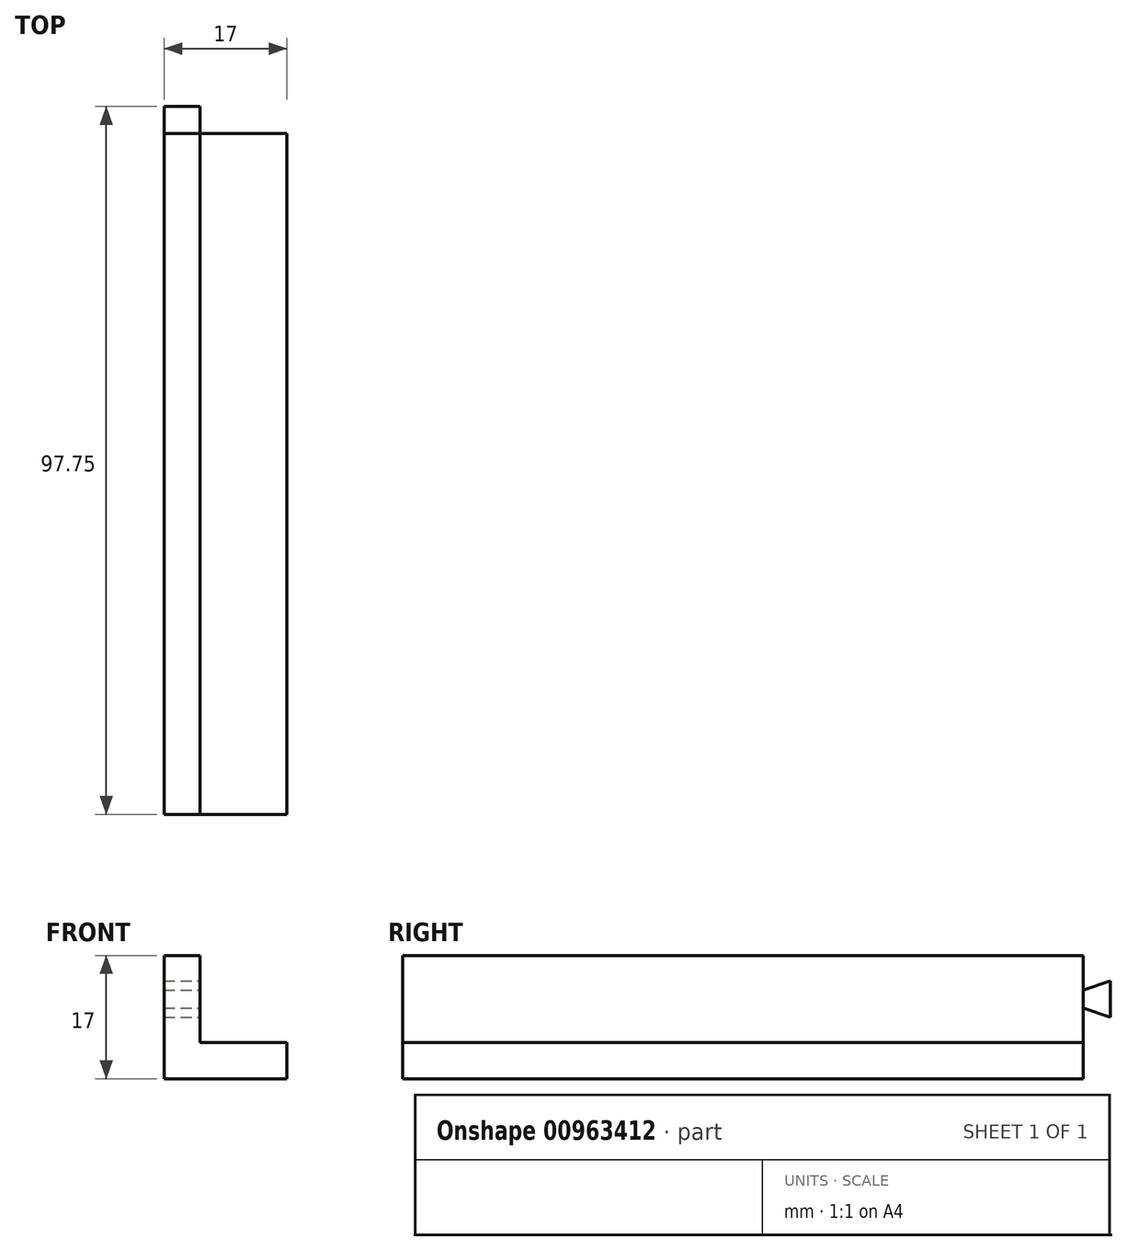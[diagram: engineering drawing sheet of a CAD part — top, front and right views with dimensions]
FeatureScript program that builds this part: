
annotation { "Feature Type Name" : "Feature", "Feature Type Description" : "" }
export const myFeature = defineFeature(function(context is Context, id is Id, definition is map)
    precondition{}
    {
        {
            var Q0;
            Q0=qCreatedBy(makeId("Top.planeOp"),FACE);
            var sketch = newSketch(context, id + "F0", { "sketchPlane" : qUnion([Q0])});
            skLineSegment(sketch, "E0.bottom", {"start": v(8.5, -47) * mm, "end": v(-8.5, -47) * mm});
            skLineSegment(sketch, "E0.top", {"start": v(8.5, 47) * mm, "end": v(-8.5, 47) * mm});
            skLineSegment(sketch, "E0.left", {"start": v(8.5, -47) * mm, "end": v(8.5, 47) * mm});
            skLineSegment(sketch, "E0.right", {"start": v(-8.5, -47) * mm, "end": v(-8.5, 47) * mm});
            skPoint(sketch, "E0.middle", {"position": v(0, 0) * mm});
            skLineSegment(sketch, "E1", {"start": v(3.75, 47) * mm, "end": v(1.25, 47) * mm});
            skSolve(sketch);
        }
        {
            var Q0;
            Q0=makeQuery(id+"F0.imprint","IMPRINT",FACE,{"disambiguationData":[TD([[makeQuery(id+"F0.imprint","IMPRINT",EDGE,{"derivedFrom":sQuery(id+"F0.wireOp",EDGE,"E0.bottom")}),-1.0]])]});
            extrude(context, id + "F1", {"entities" : qUnion([Q0]), "depth" : 5 * mm, "offsetDistance" : 25 * mm});
        }
        {
            var Q0;
            Q0=makeQuery(id+"F1.opExtrude","CAP_FACE",FACE,{"disambiguationData":[OSD([sQuery(id+"F0.wireOp",EDGE,"E0.bottom"),sQuery(id+"F0.wireOp",EDGE,"E0.top"),sQuery(id+"F0.wireOp",EDGE,"E0.left"),sQuery(id+"F0.wireOp",EDGE,"E0.right"),sQuery(id+"F0.wireOp",EDGE,"rw5FdkIU-7Pyv-DcX8-fDZG-QsmjpqUQaUpg"),sQuery(id+"F0.wireOp",EDGE,"jVwzFZEz-LamF-PFxA-NCYc-S7eYUaHMYtTf"),sQuery(id+"F0.wireOp",EDGE,"HgkX7Yv0-hTDJ-ucJP-wwuC-oNEPRnFH2NnW"),sQuery(id+"F0.wireOp",EDGE,"0Pd2xpSO-AvzK-sIeG-jRaa-LW2rH33TRvBc")])],"isStart":false});
            var sketch = newSketch(context, id + "F2", { "sketchPlane" : qUnion([Q0])});
            skLineSegment(sketch, "E2.bottom", {"start": v(-8.5, 47) * mm, "end": v(-3.5, 47) * mm});
            skLineSegment(sketch, "E2.top", {"start": v(-8.5, -47) * mm, "end": v(-3.5, -47) * mm});
            skLineSegment(sketch, "E2.left", {"start": v(-8.5, 47) * mm, "end": v(-8.5, -47) * mm});
            skLineSegment(sketch, "E2.right", {"start": v(-3.5, 47) * mm, "end": v(-3.5, -47) * mm});
            skSolve(sketch);
        }
        {
            var Q0;
            Q0=makeQuery(id+"F2.imprint","IMPRINT",FACE,{"disambiguationData":[TD([[makeQuery(id+"F2.imprint","IMPRINT",EDGE,{"derivedFrom":sQuery(id+"F2.wireOp",EDGE,"E2.bottom")}),1.0]])]});
            extrude(context, id + "F3", {"entities" : qUnion([Q0]), "operationType" : NewBodyOperationType.ADD, "depth" : 12 * mm, "offsetDistance" : 25 * mm});
        }
        {
            var Q0;
            Q0=makeQuery(id+"F3.opExtrude","SWEPT_FACE",FACE,{"disambiguationData":[OSD([sQuery(id+"F2.wireOp",EDGE,"E2.right")])]});
            var sketch = newSketch(context, id + "F4", { "sketchPlane" : qUnion([Q0])});
            skLineSegment(sketch, "E3", {"start": v(47, 17) * mm, "end": v(47, 5) * mm, "construction": true});
            skPoint(sketch, "E4", {"position": v(47, 12.25) * mm});
            skLineSegment(sketch, "E5.MirrorCS", {"start": v(47, 12.25) * mm, "end": v(50.75, 13.5) * mm});
            skLineSegment(sketch, "E6.MirrorCS", {"start": v(50.75, 8.5) * mm, "end": v(47, 9.75) * mm});
            skLineSegment(sketch, "E7", {"start": v(47, 12.25) * mm, "end": v(47, 9.75) * mm});
            skLineSegment(sketch, "E8", {"start": v(50.75, 13.5) * mm, "end": v(50.75, 8.5) * mm});
            skSolve(sketch);
        }
        {
            var Q0;
            Q0=makeQuery(id+"F4.imprint","IMPRINT",FACE,{"disambiguationData":[TD([[makeQuery(id+"F4.imprint","IMPRINT",EDGE,{"derivedFrom":sQuery(id+"F4.wireOp",EDGE,"E5.MirrorCS")}),-1.0]])]});
            extrude(context, id + "F5", {"entities" : qUnion([Q0]), "oppositeDirection" : true, "depth" : 5 * mm, "offsetDistance" : 25 * mm});
        }
    });
